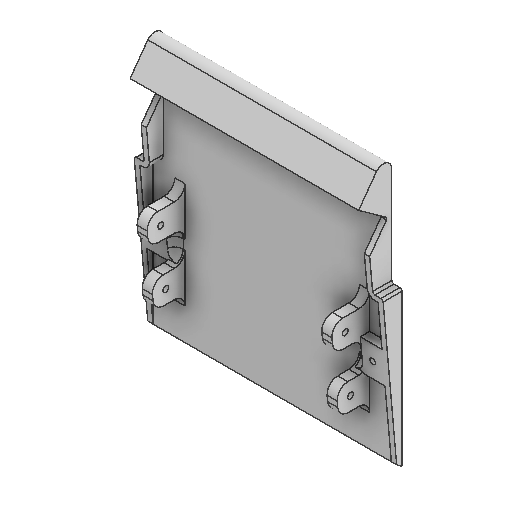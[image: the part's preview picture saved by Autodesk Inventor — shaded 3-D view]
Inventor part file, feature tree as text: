
AUTODESK INVENTOR PART (.ipt)
format: ipt  version: 2025 (Build 290162000, 162)  size: 561,664 bytes
history: native  units: mm
features: extrude x17, sketch x17, projected_geometry x15, reference x11, other x8, fillet x6, plane x4, mirror x2, thicken_offset x2, pattern_linear x1
ambient origin geometry x8: Origin, YZ Plane, XZ Plane, XY Plane, X Axis, Y Axis, Z Axis, Center Point
bodies: Solid1 (feature_tree)
feature tree (83):
  extrude  "Extrusion1"  Depth=245.0mm
  extrude  "Extrusion3"  TaperAngle=0.0deg  [1 undecoded]
  extrude  "Extrusion2"  Depth=2.0mm TaperAngle=0.0deg
  fillet  "Fillet1"  Radius=25.4mm
  sketch  "Sketch4"  dims[d12=9.525mm d13=5.0mm d14=0.0mm]
  plane  "Work Plane1"
  extrude  "Extrusion4"  Depth=5.0mm TaperAngle=0.0deg
  extrude  "Extrusion5"  Depth=9.525mm
  fillet  "Fillet2"  Radius=5.5mm
  fillet  "Fillet3"  Radius=5.5mm
  extrude  "Extrusion6"  Depth=10.0mm
  extrude  "Extrusion7"  Depth=10.0mm
  extrude  "Extrusion8"  Depth=30.0mm TaperAngle=0.0deg
  extrude  "Extrusion9"  TaperAngle=0.0deg  [1 undecoded]
  extrude  "Extrusion10"  Depth=10.0mm TaperAngle=0.0deg
  extrude  "Extrusion11"  TaperAngle=0.0deg  [1 undecoded]
  plane  "Work Plane2"
  extrude  "Extrusion12"  Depth=10.0mm
  pattern_linear  "Rectangular Pattern1"  Count1=2  [1 undecoded]
  mirror  "Mirror1"
  extrude  "Extrusion13"  Depth=10.0mm
  fillet  "Fillet4"  Radius=10.0mm
  extrude  "Extrusion14"  Depth=10.0mm
  sketch  "Sketch15"  dims[d50=10.0mm d51=0.0mm d52=5.5mm]
  plane  "Work Plane3"
  extrude  "Extrusion15"  [1 undecoded]
  extrude  "Extrusion16"  TaperAngle=0.0deg  [1 undecoded]
  plane  "Work Plane4"
  extrude  "Extrusion17"  Depth=2.0mm
  fillet  "Fillet5"  Radius=2.0mm
  mirror  "Mirror2"
  fillet  "Fillet6"  Radius=0.2mm
  thicken_offset  "Thicken1"
  thicken_offset  "Thicken2"
  sketch  "Sketch1"  dims[d0=234.0mm d1=245.0mm]
  sketch  "Sketch2"  dims[d2=5.0mm d3=0.0mm d4=0.0mm d5=0.0mm]
  projected_geometry  "Projected Loop1"
  sketch  "Sketch3"  dims[d6=2.0mm d7=5.0mm d8=0.0mm d9=25.4mm]
  projected_geometry  "Projected Loop2"
  reference  "Reference1"
  reference  "Reference2"
  reference  "Reference3"
  reference  "Reference4"
  projected_geometry  "Projected Loop3"
  reference  "Reference5"
  sketch  "Sketch5"  dims[d15=25.4mm d16=9.525mm d17=5.5mm d18=5.5mm]
  reference  "Reference6"
  sketch  "Sketch6"  dims[d19=0.0mm d20=0.0mm d21=10.0mm]
  projected_geometry  "Projected Loop4"
  sketch  "Sketch7"  dims[d22=10.0mm d23=5.0mm]
  projected_geometry  "Projected Loop5"
  projected_geometry  "Projected Loop6"
  sketch  "Sketch8"  dims[d24=5.0mm d25=30.0mm d26=0.0mm]
  reference  "Reference7"
  reference  "Reference8"
  projected_geometry  "Projected Loop7"
  reference  "Reference9"
  reference  "Reference10"
  sketch  "Sketch9"  dims[d27=0.0mm d28=0.0mm d29=0.0mm d30=0.0mm]
  projected_geometry  "Projected Loop8"
  reference  "Reference11"
  sketch  "Sketch10"  dims[d31=10.0mm d32=0.0mm d33=25.4mm d34=0.0mm]
  projected_geometry  "Projected Loop9"
  sketch  "Sketch11"  dims[d35=5.5mm d36=0.0mm d37=0.0mm]
  projected_geometry  "Projected Loop10"
  sketch  "Sketch12"  dims[d38=-5.0mm d39=10.0mm]
  sketch  "Sketch13"  dims[d40=0.0mm d41=0.0mm d42=20.0mm d44=50.0mm]
  projected_geometry  "Projected Loop11"
  projected_geometry  "Projected Loop12"
  sketch  "Sketch14"  dims[d45=0.0mm d46=0.0mm d47=8.0mm d48=10.0mm d49=0.0mm]
  projected_geometry  "Projected Loop13"
  projected_geometry  "Projected Loop14"
  sketch  "Sketch16"  dims[d53=0.0mm d54=0.0mm d55=-5.0mm]
  projected_geometry  "Projected Loop15"
  sketch  "Sketch17"  dims[d56=10.0mm d57=0.0mm d58=0.0mm d59=8.0mm d60=2.0mm d61=0.2mm d62=1.0mm d63=0.2mm d64=1.0mm]
  other  "<userpath>\Desktop\puppycat\woodhouseMK1.iam"
  other  "woodhouseMK1.iam"
  other  "trackBase:1"
  other  "6pt9inStrut:1"
  other  "swingarmBaseV4:1"
  other  "lowerUndercarriageBracket:1"
  other  "horizontalStrut:1"
  other  "frontUndercarriageBracket:1"
note: 6 required parameter values undecoded (feature->parameter linkage not recoverable at this tier; creation-order binding heuristic only, values carry confidence <= 0.55)
